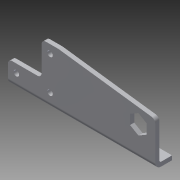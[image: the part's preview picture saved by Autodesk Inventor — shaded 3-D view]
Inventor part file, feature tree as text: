
AUTODESK INVENTOR PART (.ipt)
format: ipt  version: 2014 (Build 180170000, 170)  size: 190,976 bytes
history: native  units: in
note: dims shown in document units (in); Inventor stores cm internally (conversion verified against a paired STEP export)
features: sheet_metal_op x4, other x4, sketch x2, fillet x1
ambient origin geometry x8: Origin, YZ Plane, XZ Plane, XY Plane, X Axis, Y Axis, Z Axis, Center Point
bodies: Solid1 (feature_tree)
feature tree (11):
  sheet_metal_op  "Face1"
  sheet_metal_op  "Flange1"
  fillet  "Fillet2"  Radius=0.5in
  sketch  "Sketch1"  dims[d1=1.0in]
  other  "Plate1"
  sketch  "Sketch2"  dims[d2=1.0in d3=0.5in d4=4.375in d5=0.5in d6=0.75in d7=0.5in d8=90.0deg d9=1.125in d10=0.163in d11=0.25in d12=0.25in d13=0.7874in d15=1.0in d16=0.3937in d18=1.0in d20=0.7874in d22=1.0in d23=0.3937in d25=1.0in d27=0.125in d29=0.125in d30=0.0625in d31=0.25in d32=0.125in d33=0.5in d34=90.0deg d35=0.05in d36=0.5in d37=0.125in d38=0.125in d39=0.125in]
  other  "Plate2"
  sheet_metal_op  "Bend1"
  sheet_metal_op  "Corner1"
  other  "Definition1"
  other  "Cut1"
